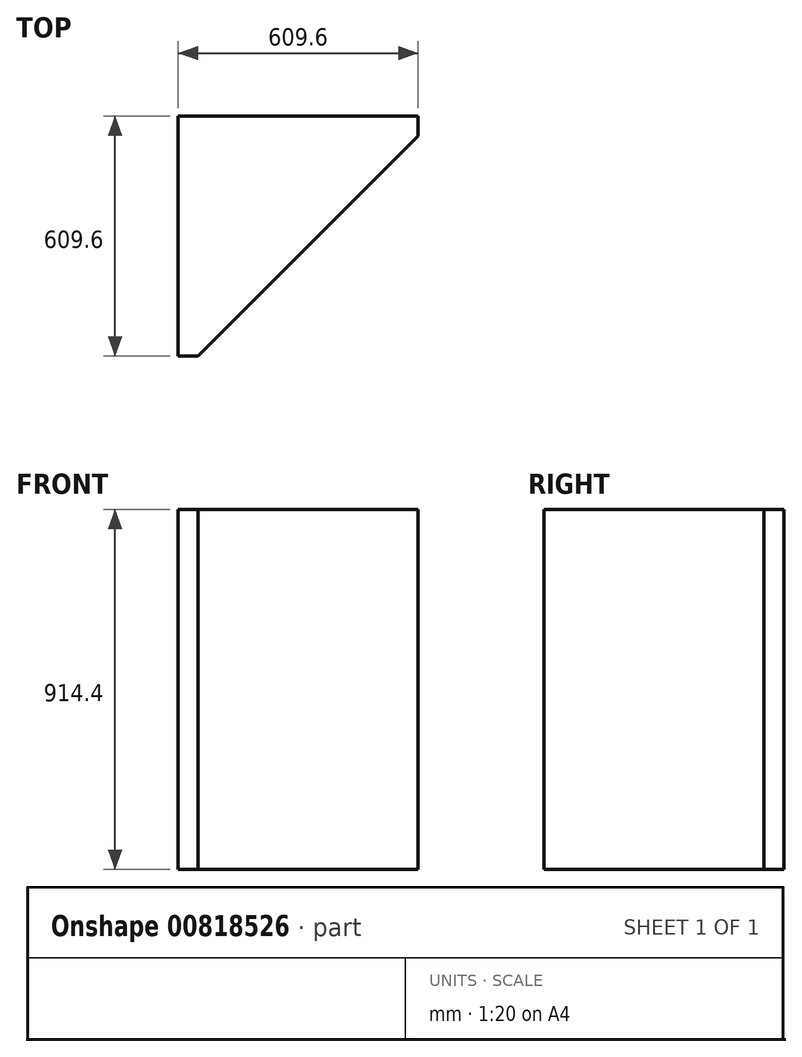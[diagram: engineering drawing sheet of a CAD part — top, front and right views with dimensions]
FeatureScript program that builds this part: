
annotation { "Feature Type Name" : "Feature", "Feature Type Description" : "" }
export const myFeature = defineFeature(function(context is Context, id is Id, definition is map)
    precondition{}
    {
        {
            var Q0;
            Q0=qCreatedBy(makeId("Top.planeOp"),FACE);
            var sketch = newSketch(context, id + "F0", { "sketchPlane" : qUnion([Q0])});
            skLineSegment(sketch, "E0", {"start": v(0, 0) * mm, "end": v(609.6, 0) * mm});
            skLineSegment(sketch, "E1", {"start": v(0, 0) * mm, "end": v(0, -609.6) * mm});
            skLineSegment(sketch, "E2", {"start": v(0, -609.6) * mm, "end": v(50.8, -609.6) * mm});
            skLineSegment(sketch, "E3", {"start": v(50.8, -609.6) * mm, "end": v(609.22, -50.8) * mm});
            skLineSegment(sketch, "E4", {"start": v(609.22, -50.8) * mm, "end": v(609.6, 0) * mm});
            skSolve(sketch);
        }
        {
            var Q0;
            Q0=makeQuery(id+"F0.imprint","IMPRINT",FACE,{"disambiguationData":[TD([[makeQuery(id+"F0.imprint","IMPRINT",EDGE,{"derivedFrom":sQuery(id+"F0.wireOp",EDGE,"E0")}),-1.0]])]});
            extrude(context, id + "F1", {"entities" : qUnion([Q0]), "depth" : 914.4 * mm, "offsetDistance" : 25.4 * mm});
        }
    });
